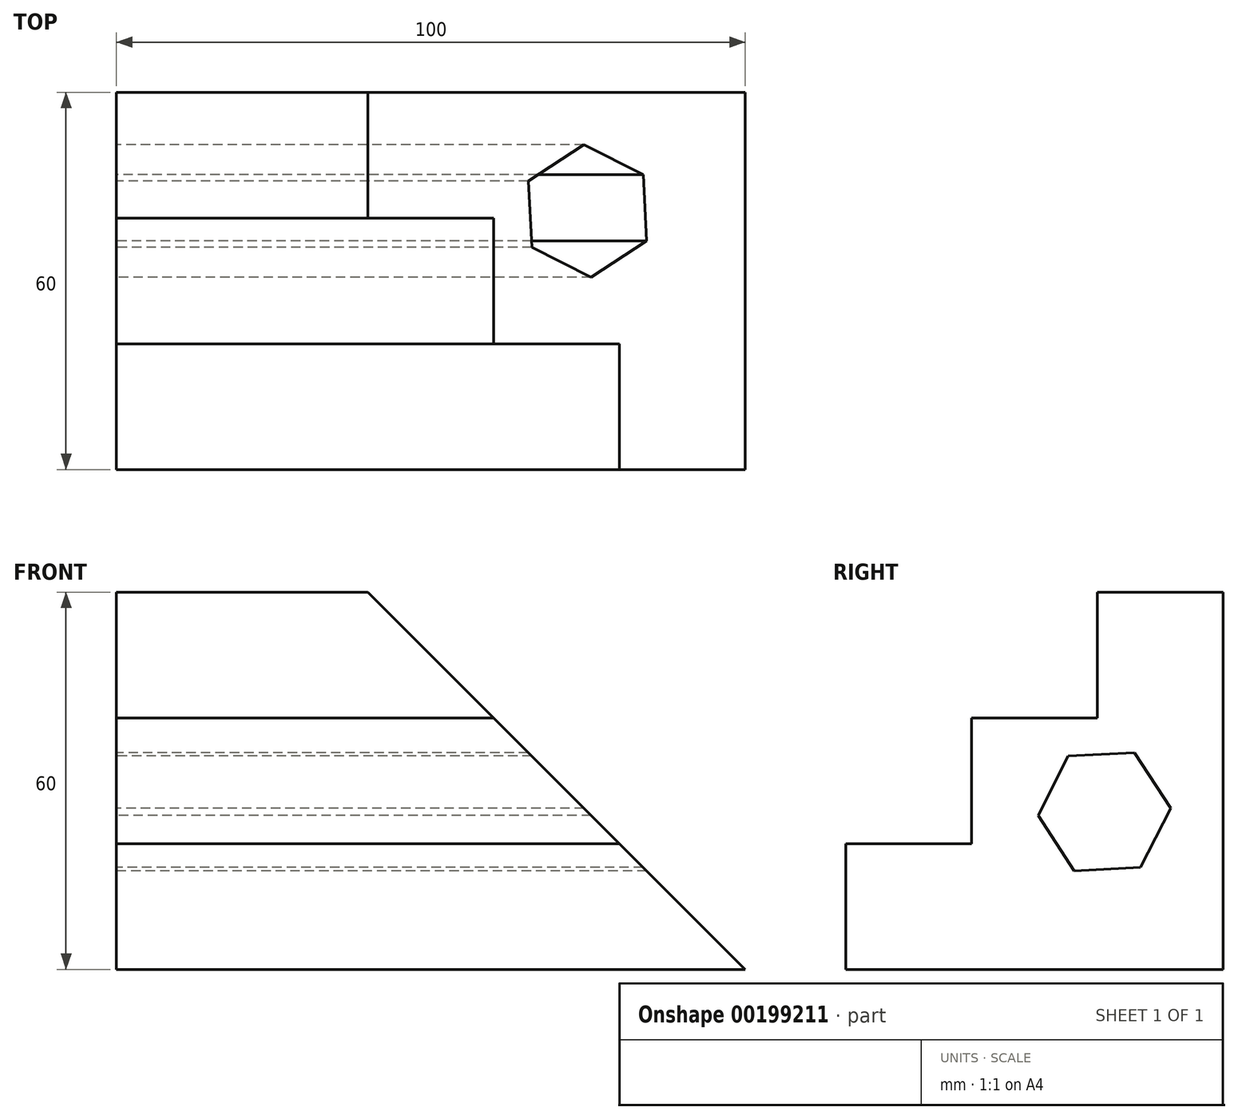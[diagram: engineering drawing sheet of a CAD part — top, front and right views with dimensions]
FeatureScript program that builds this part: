
annotation { "Feature Type Name" : "Feature", "Feature Type Description" : "" }
export const myFeature = defineFeature(function(context is Context, id is Id, definition is map)
    precondition{}
    {
        {
            var Q0;
            Q0=qCreatedBy(makeId("Right.planeOp"),FACE);
            var sketch = newSketch(context, id + "F0", { "sketchPlane" : qUnion([Q0])});
            skLineSegment(sketch, "E0", {"start": v(0, 0) * mm, "end": v(0, 20) * mm});
            skLineSegment(sketch, "E1", {"start": v(0, 20) * mm, "end": v(20, 20) * mm});
            skLineSegment(sketch, "E2", {"start": v(20, 20) * mm, "end": v(20, 40) * mm});
            skLineSegment(sketch, "E3", {"start": v(20, 40) * mm, "end": v(40, 40) * mm});
            skLineSegment(sketch, "E4", {"start": v(40, 40) * mm, "end": v(40, 60) * mm});
            skLineSegment(sketch, "E5", {"start": v(40, 60) * mm, "end": v(60, 60) * mm});
            skLineSegment(sketch, "E6", {"start": v(60, 60) * mm, "end": v(60, 0) * mm});
            skLineSegment(sketch, "E7", {"start": v(60, 0) * mm, "end": v(0, 0) * mm});
            skSolve(sketch);
        }
        {
            var Q0;
            Q0=makeQuery(id+"F0.imprint","IMPRINT",FACE,{"disambiguationData":[TD([[makeQuery(id+"F0.imprint","IMPRINT",EDGE,{"derivedFrom":sQuery(id+"F0.wireOp",EDGE,"E0")}),-1.0]])]});
            extrude(context, id + "F1", {"entities" : qUnion([Q0]), "depth" : 100 * mm});
        }
        {
            var Q0;
            Q0=makeQuery(id+"F1.opExtrude","SWEPT_FACE",FACE,{"disambiguationData":[OSD([sQuery(id+"F0.wireOp",EDGE,"E6")])]});
            var sketch = newSketch(context, id + "F2", { "sketchPlane" : qUnion([Q0])});
            skLineSegment(sketch, "E8", {"start": v(-100, 0) * mm, "end": v(-40, 60) * mm});
            skSolve(sketch);
        }
        {
            var Q0;
            {var subQ0=sQuery(id+"F2.wireOp",EDGE,"E8");Q0=makeQuery(id+"F2.imprint","IMPRINT",FACE,{"disambiguationData":[TD([[makeQuery(id+"F2.imprint","IMPRINT",EDGE,{"derivedFrom":subQ0}),1.0]])]});}
            extrude(context, id + "F3", {"entities" : qUnion([Q0]), "operationType" : NewBodyOperationType.REMOVE, "endBound" : BoundingType.THROUGH_ALL, "oppositeDirection" : true, "depth" : 25 * mm});
        }
        {
            var Q0;
            Q0=makeQuery(id+"F1.opExtrude","CAP_FACE",FACE,{"disambiguationData":[OSD([sQuery(id+"F0.wireOp",EDGE,"E0"),sQuery(id+"F0.wireOp",EDGE,"E1"),sQuery(id+"F0.wireOp",EDGE,"E2"),sQuery(id+"F0.wireOp",EDGE,"E3"),sQuery(id+"F0.wireOp",EDGE,"E4"),sQuery(id+"F0.wireOp",EDGE,"E5"),sQuery(id+"F0.wireOp",EDGE,"E6"),sQuery(id+"F0.wireOp",EDGE,"E7")])],"isStart":true});
            var sketch = newSketch(context, id + "F4", { "sketchPlane" : qUnion([Q0])});
            skCircle(sketch, "E9.cCircle", {"center": v(-41.13, 25.07) * mm, "radius": 10.56 * mm, "construction": true});
            skLineSegment(sketch, "E9.0", {"start": v(-35.37, 33.92) * mm, "end": v(-30.59, 24.51) * mm});
            skLineSegment(sketch, "E9.1", {"start": v(-30.59, 24.51) * mm, "end": v(-36.34, 15.66) * mm});
            skLineSegment(sketch, "E9.2", {"start": v(-36.34, 15.66) * mm, "end": v(-46.89, 16.23) * mm});
            skLineSegment(sketch, "E9.3", {"start": v(-46.89, 16.23) * mm, "end": v(-51.67, 25.64) * mm});
            skLineSegment(sketch, "E9.4", {"start": v(-51.67, 25.64) * mm, "end": v(-45.91, 34.48) * mm});
            skLineSegment(sketch, "E9.5", {"start": v(-45.91, 34.48) * mm, "end": v(-35.37, 33.92) * mm});
            skSolve(sketch);
        }
        {
            var Q0;
            Q0=makeQuery(id+"F4.imprint","IMPRINT",FACE,{"disambiguationData":[TD([[makeQuery(id+"F4.imprint","IMPRINT",EDGE,{"derivedFrom":sQuery(id+"F4.wireOp",EDGE,"E9.0")}),-1.0]])]});
            extrude(context, id + "F5", {"entities" : qUnion([Q0]), "operationType" : NewBodyOperationType.REMOVE, "endBound" : BoundingType.THROUGH_ALL, "oppositeDirection" : true, "depth" : 25 * mm});
        }
    });
